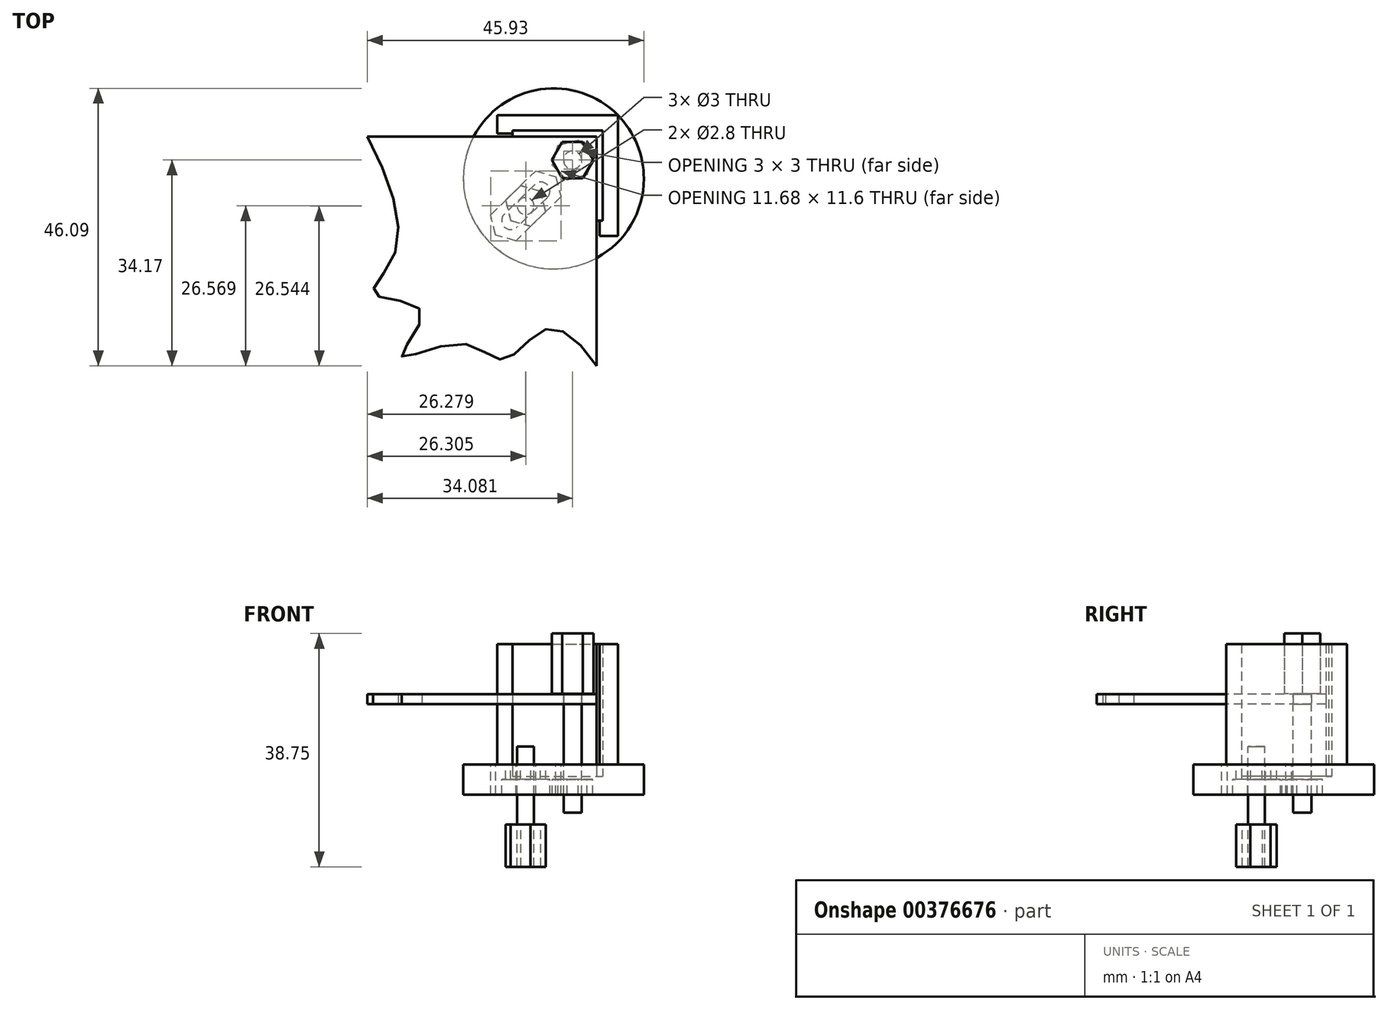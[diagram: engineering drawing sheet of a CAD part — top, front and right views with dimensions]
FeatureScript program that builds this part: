
annotation { "Feature Type Name" : "Feature", "Feature Type Description" : "" }
export const myFeature = defineFeature(function(context is Context, id is Id, definition is map)
    precondition{}
    {
        {
            var Q0;
            Q0=qCreatedBy(makeId("Top.planeOp"),FACE);
            var sketch = newSketch(context, id + "F0", { "sketchPlane" : qUnion([Q0])});
            skCircle(sketch, "E0", {"center": v(0, 0) * mm, "radius": 15 * mm});
            skLineSegment(sketch, "E1.bottom", {"start": v(-6.85, 7.99) * mm, "end": v(8.15, 7.99) * mm});
            skLineSegment(sketch, "E1.right", {"start": v(8.15, 7.99) * mm, "end": v(8.15, -7.01) * mm});
            skLineSegment(sketch, "E2.0", {"start": v(7.15, 6.99) * mm, "end": v(7.15, -7.01) * mm});
            skLineSegment(sketch, "E2.1", {"start": v(-6.85, 6.99) * mm, "end": v(7.15, 6.99) * mm});
            skLineSegment(sketch, "E3", {"start": v(-2.12, -2.07) * mm, "end": v(-7.13, -6.97) * mm, "construction": true});
            skArc(sketch, "E4.0.startCap", {"start": v(-3.17, -1) * mm, "mid": v(-1.05, -1.03) * mm, "end": v(-1.07, -3.15) * mm});
            skArc(sketch, "E4.0.endCap", {"start": v(-6.08, -8.04) * mm, "mid": v(-8.2, -8.02) * mm, "end": v(-8.18, -5.9) * mm});
            skLineSegment(sketch, "E4.0.left", {"start": v(-1.07, -3.15) * mm, "end": v(-6.08, -8.04) * mm});
            skLineSegment(sketch, "E4.0.right", {"start": v(-3.17, -1) * mm, "end": v(-8.18, -5.9) * mm});
            skLineSegment(sketch, "E5", {"start": v(0.02, 0.02) * mm, "end": v(17.55, 17.15) * mm, "construction": true});
            skLineSegment(sketch, "E6", {"start": v(-6.85, 6.99) * mm, "end": v(-6.85, 7.99) * mm});
            skLineSegment(sketch, "E7", {"start": v(7.15, -7.01) * mm, "end": v(8.15, -7.01) * mm});
            skLineSegment(sketch, "E8.0", {"start": v(-9.38, 7.49) * mm, "end": v(-9.38, 10.52) * mm});
            skLineSegment(sketch, "E8.1", {"start": v(10.69, 10.52) * mm, "end": v(10.69, -9.55) * mm});
            skLineSegment(sketch, "E8.2", {"start": v(7.65, -9.55) * mm, "end": v(10.69, -9.55) * mm});
            skLineSegment(sketch, "E8.3", {"start": v(-9.38, 10.52) * mm, "end": v(10.69, 10.52) * mm});
            skPoint(sketch, "E9.endSnap0", {"position": v(-9.38, 7.49) * mm});
            skPoint(sketch, "E10.orphan", {"position": v(-9.38, 4.45) * mm});
            skLineSegment(sketch, "E11", {"start": v(7.65, -7.01) * mm, "end": v(7.65, -9.55) * mm});
            skLineSegment(sketch, "E12", {"start": v(-6.85, 7.49) * mm, "end": v(-9.38, 7.49) * mm});
            skPoint(sketch, "E9.end.orphan", {"position": v(-9.38, 7.07) * mm});
            skLineSegment(sketch, "E13", {"start": v(-2.12, -2.07) * mm, "end": v(0, 0) * mm, "construction": true});
            skCircle(sketch, "E14", {"center": v(3.15, 3.08) * mm, "radius": 1.5 * mm});
            skCircle(sketch, "E15.cCircle", {"center": v(-7.13, -6.97) * mm, "radius": 3 * mm, "construction": true});
            skLineSegment(sketch, "E15.0", {"start": v(-5.03, -9.11) * mm, "end": v(-6.27, -10.32) * mm});
            skLineSegment(sketch, "E15.1", {"start": v(-6.27, -10.32) * mm, "end": v(-9.6, -9.39) * mm});
            skLineSegment(sketch, "E15.2", {"start": v(-9.6, -9.39) * mm, "end": v(-10.46, -6.03) * mm});
            skLineSegment(sketch, "E15.3", {"start": v(-10.46, -6.03) * mm, "end": v(-9.23, -4.82) * mm});
            skPoint(sketch, "E15.0.midPoint", {"position": v(-5.03, -9.11) * mm});
            skCircle(sketch, "E16.cCircle", {"center": v(-2.12, -2.07) * mm, "radius": 3 * mm, "construction": true});
            skLineSegment(sketch, "E16.0", {"start": v(1.21, -3) * mm, "end": v(-0.03, -4.22) * mm});
            skLineSegment(sketch, "E16.3", {"start": v(-4.22, 0.07) * mm, "end": v(-2.98, 1.28) * mm});
            skLineSegment(sketch, "E16.4", {"start": v(-2.98, 1.28) * mm, "end": v(0.36, 0.35) * mm});
            skLineSegment(sketch, "E16.5", {"start": v(0.36, 0.35) * mm, "end": v(1.21, -3) * mm});
            skPoint(sketch, "E16.0.midPoint", {"position": v(-0.03, -4.22) * mm});
            skPoint(sketch, "E17.orphan", {"position": v(-4.65, -4.55) * mm});
            skPoint(sketch, "E18.orphan", {"position": v(-3.8, -7.9) * mm});
            skLineSegment(sketch, "E19", {"start": v(-9.23, -4.82) * mm, "end": v(-4.22, 0.07) * mm});
            skLineSegment(sketch, "E20", {"start": v(-5.03, -9.11) * mm, "end": v(-0.03, -4.22) * mm});
            skSolve(sketch);
        }
        {
            var Q0;
            {var subQ4=sQuery(id+"F0.wireOp",EDGE,"E1.bottom");Q0=makeQuery(id+"F0.imprint","IMPRINT",FACE,{"disambiguationData":[TD([[makeQuery(id+"F0.imprint","IMPRINT",EDGE,{"derivedFrom":subQ4}),1.0]])]});}
            var Q1;
            Q1=makeQuery(id+"F0.imprint","IMPRINT",FACE,{"disambiguationData":[TD([[makeQuery(id+"F0.imprint","IMPRINT",EDGE,{"derivedFrom":sQuery(id+"F0.wireOp",EDGE,"E0")}),1.0]])]});
            var Q2;
            {var subQ3=sQuery(id+"F0.wireOp",EDGE,"E1.bottom");Q2=makeQuery(id+"F0.imprint","IMPRINT",FACE,{"disambiguationData":[TD([[makeQuery(id+"F0.imprint","IMPRINT",EDGE,{"derivedFrom":subQ3}),-1.0]])]});}
            var Q3;
            Q3=makeQuery(id+"F0.imprint","IMPRINT",FACE,{"disambiguationData":[TD([[makeQuery(id+"F0.imprint","IMPRINT",EDGE,{"derivedFrom":sQuery(id+"F0.wireOp",EDGE,"E4.0.startCap")}),1.0]])]});
            extrude(context, id + "F1", {"entities" : qUnion([Q0, Q1, Q2, Q3]), "oppositeDirection" : true, "depth" : 5 * mm, "offsetDistance" : 25 * mm});
        }
        {
            var Q0;
            {var subQ4=sQuery(id+"F0.wireOp",EDGE,"E1.bottom");Q0=makeQuery(id+"F0.imprint","IMPRINT",FACE,{"disambiguationData":[TD([[makeQuery(id+"F0.imprint","IMPRINT",EDGE,{"derivedFrom":subQ4}),1.0]])]});}
            extrude(context, id + "F2", {"entities" : qUnion([Q0]), "operationType" : NewBodyOperationType.ADD, "depth" : 20 * mm, "offsetDistance" : 25 * mm});
        }
        {
            var Q0;
            {var subQ3=sQuery(id+"F0.wireOp",EDGE,"E1.bottom");Q0=makeQuery(id+"F0.imprint","IMPRINT",FACE,{"disambiguationData":[TD([[makeQuery(id+"F0.imprint","IMPRINT",EDGE,{"derivedFrom":subQ3}),-1.0]])]});}
            extrude(context, id + "F3", {"entities" : qUnion([Q0]), "depth" : 20 * mm, "offsetDistance" : 25 * mm, "hasSecondDirection" : true, "secondDirectionOppositeDirection" : true, "secondDirectionDepth" : 2 * mm});
        }
        {
            var Q0;
            Q0=makeQuery(id+"F1.opExtrude","CAP_FACE",FACE,{"disambiguationData":[OSD([sQuery(id+"F0.wireOp",EDGE,"E0"),sQuery(id+"F0.wireOp",EDGE,"E4.0.startCap"),sQuery(id+"F0.wireOp",EDGE,"E4.0.endCap"),sQuery(id+"F0.wireOp",EDGE,"E4.0.left"),sQuery(id+"F0.wireOp",EDGE,"E4.0.right"),sQuery(id+"F0.wireOp",EDGE,"E14")])],"isStart":false});
            var sketch = newSketch(context, id + "F4", { "sketchPlane" : qUnion([Q0])});
            skPoint(sketch, "E21", {"position": v(3.15, -3.08) * mm});
            skCircle(sketch, "E22.cCircle", {"center": v(3.15, -3.08) * mm, "radius": 3 * mm, "construction": true});
            skLineSegment(sketch, "E22.0", {"start": v(6.5, -3.95) * mm, "end": v(4.07, -6.42) * mm});
            skLineSegment(sketch, "E22.1", {"start": v(4.07, -6.42) * mm, "end": v(0.72, -5.55) * mm});
            skLineSegment(sketch, "E22.2", {"start": v(0.72, -5.55) * mm, "end": v(-0.2, -2.2) * mm});
            skLineSegment(sketch, "E22.3", {"start": v(-0.2, -2.2) * mm, "end": v(2.23, 0.26) * mm});
            skLineSegment(sketch, "E22.4", {"start": v(2.23, 0.26) * mm, "end": v(5.58, -0.61) * mm});
            skLineSegment(sketch, "E22.5", {"start": v(5.58, -0.61) * mm, "end": v(6.5, -3.95) * mm});
            skPoint(sketch, "E22.0.midPoint", {"position": v(5.29, -5.19) * mm});
            skSolve(sketch);
        }
        {
            var Q0;
            Q0=makeQuery(id+"F4.imprint","IMPRINT",FACE,{"disambiguationData":[TD([[makeQuery(id+"F4.imprint","IMPRINT",EDGE,{"derivedFrom":sQuery(id+"F4.wireOp",EDGE,"E22.0")}),-1.0]])]});
            extrude(context, id + "F5", {"entities" : qUnion([Q0]), "operationType" : NewBodyOperationType.REMOVE, "oppositeDirection" : true, "depth" : 2.5 * mm, "offsetDistance" : 25 * mm});
        }
        {
            var Q0;
            Q0=makeQuery(id+"F0.imprint","IMPRINT",FACE,{"disambiguationData":[TD([[makeQuery(id+"F0.imprint","IMPRINT",EDGE,{"derivedFrom":sQuery(id+"F0.wireOp",EDGE,"E4.0.startCap")}),1.0]])]});
            extrude(context, id + "F6", {"entities" : qUnion([Q0]), "operationType" : NewBodyOperationType.REMOVE, "oppositeDirection" : true, "depth" : 2.5 * mm, "offsetDistance" : 25 * mm});
        }
        {
            var Q0;
            Q0=makeQuery(id+"F0.imprint","IMPRINT",FACE,{"disambiguationData":[TD([[makeQuery(id+"F0.imprint","IMPRINT",EDGE,{"derivedFrom":sQuery(id+"F0.wireOp",EDGE,"E0")}),1.0]])]});
            cPlane(context, id + "F7", {"entities" : qUnion([Q0]), "cplaneType" : CPlaneType.OFFSET, "offset" : 10 * mm, "width" : 150 * mm, "height" : 150 * mm});
        }
        {
            var Q0;
            Q0=qCreatedBy(id+"F7.planeOp",FACE);
            var sketch = newSketch(context, id + "F8", { "sketchPlane" : qUnion([Q0])});
            skLineSegment(sketch, "E23.bottom", {"start": v(7.15, 6.99) * mm, "end": v(-30.93, 6.99) * mm});
            skLineSegment(sketch, "E23.left", {"start": v(7.15, 6.99) * mm, "end": v(7.15, -31.1) * mm});
            skFitSpline(sketch, "E24", {"points": [v(-30.93, 6.99) * mm, v(-26.55, -12.85) * mm, v(-29.76, -19.17) * mm, v(-21.98, -22.11) * mm, v(-25.26, -29.41) * mm, v(-15.4, -27.41) * mm, v(-8.13, -30.02) * mm, v(-1.2, -25.01) * mm, v(7.15, -31.1) * mm], "startDerivative": vector(61.2, -118.32) * mm, "endDerivative": vector(56.82, -85.75) * mm});
            skCircle(sketch, "E25.0", {"center": v(3.15, 3.08) * mm, "radius": 1.5 * mm});
            skSolve(sketch);
        }
        {
            var Q0;
            Q0=makeQuery(id+"F8.imprint","IMPRINT",FACE,{"disambiguationData":[TD([[makeQuery(id+"F8.imprint","IMPRINT",EDGE,{"derivedFrom":sQuery(id+"F8.wireOp",EDGE,"E23.bottom")}),1.0]])]});
            extrude(context, id + "F9", {"entities" : qUnion([Q0]), "depth" : 1.7 * mm, "offsetDistance" : 25 * mm});
        }
        {
            var Q0;
            Q0=makeQuery(id+"F0.imprint","IMPRINT",FACE,{"disambiguationData":[TD([[makeQuery(id+"F0.imprint","IMPRINT",EDGE,{"derivedFrom":sQuery(id+"F0.wireOp",EDGE,"E0")}),1.0]])]});
            var sketch = newSketch(context, id + "F10", { "sketchPlane" : qUnion([Q0])});
            skPoint(sketch, "E26.0", {"position": v(-4.65, -4.55) * mm});
            skCircle(sketch, "E27", {"center": v(-4.65, -4.55) * mm, "radius": 1.4 * mm});
            skCircle(sketch, "E28.cCircle", {"center": v(-4.65, -4.55) * mm, "radius": 3 * mm, "construction": true});
            skLineSegment(sketch, "E28.0", {"start": v(-1.32, -5.48) * mm, "end": v(-3.8, -7.9) * mm});
            skLineSegment(sketch, "E28.1", {"start": v(-3.8, -7.9) * mm, "end": v(-7.13, -6.97) * mm});
            skLineSegment(sketch, "E28.2", {"start": v(-7.13, -6.97) * mm, "end": v(-7.99, -3.61) * mm});
            skLineSegment(sketch, "E28.3", {"start": v(-7.99, -3.61) * mm, "end": v(-5.5, -1.19) * mm});
            skLineSegment(sketch, "E28.4", {"start": v(-5.5, -1.19) * mm, "end": v(-2.17, -2.12) * mm});
            skLineSegment(sketch, "E28.5", {"start": v(-2.17, -2.12) * mm, "end": v(-1.32, -5.48) * mm});
            skPoint(sketch, "E28.0.midPoint", {"position": v(-2.58, -6.67) * mm});
            skSolve(sketch);
        }
        {
            var Q0;
            Q0 = qSketchRegion(id + "F10", true);
            var Q1;
            Q1=makeQuery(id+"F6.boolean.opBoolean","COPY",FACE,{"derivedFrom":makeQuery(id+"F6.opExtrude","CAP_FACE",FACE,{"disambiguationData":[OSD([sQuery(id+"F0.wireOp",EDGE,"E4.0.startCap"),sQuery(id+"F0.wireOp",EDGE,"E4.0.endCap"),sQuery(id+"F0.wireOp",EDGE,"E4.0.left"),sQuery(id+"F0.wireOp",EDGE,"E4.0.right"),sQuery(id+"F0.wireOp",EDGE,"E15.0"),sQuery(id+"F0.wireOp",EDGE,"E15.1"),sQuery(id+"F0.wireOp",EDGE,"E15.2"),sQuery(id+"F0.wireOp",EDGE,"E15.3"),sQuery(id+"F0.wireOp",EDGE,"E16.0"),sQuery(id+"F0.wireOp",EDGE,"E16.3"),sQuery(id+"F0.wireOp",EDGE,"E16.4"),sQuery(id+"F0.wireOp",EDGE,"E16.5"),sQuery(id+"F0.wireOp",EDGE,"E19"),sQuery(id+"F0.wireOp",EDGE,"E20")])],"isStart":false})});
            extrude(context, id + "F11", {"entities" : qUnion([Q0]), "endBound" : BoundingType.UP_TO_SURFACE, "oppositeDirection" : true, "depth" : 25 * mm, "endBoundEntityFace" : qUnion([Q1]), "offsetDistance" : 25 * mm});
        }
        {
            var Q0;
            Q0=makeQuery(id+"F0.imprint","IMPRINT",FACE,{"disambiguationData":[TD([[makeQuery(id+"F0.imprint","IMPRINT",EDGE,{"derivedFrom":sQuery(id+"F0.wireOp",EDGE,"E0")}),1.0]])]});
            var sketch = newSketch(context, id + "F12", { "sketchPlane" : qUnion([Q0])});
            skCircle(sketch, "E29.0", {"center": v(-4.65, -4.55) * mm, "radius": 1.4 * mm});
            skSolve(sketch);
        }
        {
            var Q0;
            Q0=makeQuery(id+"F12.imprint","IMPRINT",FACE,{"disambiguationData":[TD([[makeQuery(id+"F12.imprint","IMPRINT",EDGE,{"derivedFrom":sQuery(id+"F12.wireOp",EDGE,"E29.0")}),1.0]])]});
            extrude(context, id + "F13", {"entities" : qUnion([Q0]), "oppositeDirection" : true, "depth" : 10 * mm, "offsetDistance" : 25 * mm, "hasSecondDirection" : true, "secondDirectionOppositeDirection" : false, "secondDirectionDepth" : 3 * mm});
        }
        {
            var Q0;
            Q0=makeQuery(id+"F13.opExtrude","CAP_FACE",FACE,{"disambiguationData":[OSD([sQuery(id+"F12.wireOp",EDGE,"E29.0")])],"isStart":false});
            var sketch = newSketch(context, id + "F14", { "sketchPlane" : qUnion([Q0])});
            skCircle(sketch, "E30.cCircle", {"center": v(-4.65, 4.55) * mm, "radius": 3 * mm, "construction": true});
            skLineSegment(sketch, "E30.0", {"start": v(-3.85, 7.92) * mm, "end": v(-1.33, 5.54) * mm});
            skLineSegment(sketch, "E30.1", {"start": v(-1.33, 5.54) * mm, "end": v(-2.13, 2.17) * mm});
            skLineSegment(sketch, "E30.2", {"start": v(-2.13, 2.17) * mm, "end": v(-5.45, 1.17) * mm});
            skLineSegment(sketch, "E30.3", {"start": v(-5.45, 1.17) * mm, "end": v(-7.97, 3.55) * mm});
            skLineSegment(sketch, "E30.4", {"start": v(-7.97, 3.55) * mm, "end": v(-7.17, 6.92) * mm});
            skLineSegment(sketch, "E30.5", {"start": v(-7.17, 6.92) * mm, "end": v(-3.85, 7.92) * mm});
            skPoint(sketch, "E30.0.midPoint", {"position": v(-2.6, 6.73) * mm});
            skSolve(sketch);
        }
        {
            var Q0;
            Q0=makeQuery(id+"F14.imprint","IMPRINT",FACE,{"disambiguationData":[TD([[makeQuery(id+"F14.imprint","IMPRINT",EDGE,{"derivedFrom":sQuery(id+"F14.wireOp",EDGE,"E30.0")}),-1.0]])]});
            extrude(context, id + "F15", {"entities" : qUnion([Q0]), "operationType" : NewBodyOperationType.ADD, "depth" : 7 * mm, "offsetDistance" : 25 * mm});
        }
        {
            var Q0;
            Q0=makeQuery(id+"F5.boolean.opBoolean","COPY",FACE,{"derivedFrom":makeQuery(id+"F5.opExtrude","CAP_FACE",FACE,{"disambiguationData":[OSD([sQuery(id+"F0.wireOp",EDGE,"E14"),sQuery(id+"F4.wireOp",EDGE,"E22.0"),sQuery(id+"F4.wireOp",EDGE,"E22.1"),sQuery(id+"F4.wireOp",EDGE,"E22.2"),sQuery(id+"F4.wireOp",EDGE,"E22.3"),sQuery(id+"F4.wireOp",EDGE,"E22.4"),sQuery(id+"F4.wireOp",EDGE,"E22.5")])],"isStart":false})});
            var Q1;
            Q1=makeQuery(id+"F1.opExtrude","CAP_FACE",FACE,{"disambiguationData":[OSD([sQuery(id+"F0.wireOp",EDGE,"E0"),sQuery(id+"F0.wireOp",EDGE,"E4.0.startCap"),sQuery(id+"F0.wireOp",EDGE,"E4.0.endCap"),sQuery(id+"F0.wireOp",EDGE,"E4.0.left"),sQuery(id+"F0.wireOp",EDGE,"E4.0.right"),sQuery(id+"F0.wireOp",EDGE,"E14")])],"isStart":false});
            extrude(context, id + "F16", {"entities" : qUnion([Q0]), "endBound" : BoundingType.UP_TO_SURFACE, "depth" : 25 * mm, "endBoundEntityFace" : qUnion([Q1]), "offsetDistance" : 25 * mm});
        }
        {
            var Q0;
            Q0=makeQuery(id+"F1.opExtrude","CAP_FACE",FACE,{"disambiguationData":[OSD([sQuery(id+"F0.wireOp",EDGE,"E0"),sQuery(id+"F0.wireOp",EDGE,"E4.0.startCap"),sQuery(id+"F0.wireOp",EDGE,"E4.0.endCap"),sQuery(id+"F0.wireOp",EDGE,"E4.0.left"),sQuery(id+"F0.wireOp",EDGE,"E4.0.right"),sQuery(id+"F0.wireOp",EDGE,"E14")])],"isStart":false});
            var sketch = newSketch(context, id + "F17", { "sketchPlane" : qUnion([Q0])});
            skCircle(sketch, "E31.0", {"center": v(3.15, -3.08) * mm, "radius": 1.5 * mm});
            skSolve(sketch);
        }
        {
            var Q0;
            Q0=makeQuery(id+"F17.imprint","IMPRINT",FACE,{"disambiguationData":[TD([[makeQuery(id+"F17.imprint","IMPRINT",EDGE,{"derivedFrom":sQuery(id+"F17.wireOp",EDGE,"E31.0")}),1.0]])]});
            extrude(context, id + "F18", {"entities" : qUnion([Q0]), "depth" : 3 * mm, "offsetDistance" : 25 * mm, "hasSecondDirection" : true, "secondDirectionOppositeDirection" : true, "secondDirectionDepth" : 16.75 * mm});
        }
        {
            var Q0;
            Q0=makeQuery(id+"F18.opExtrude","CAP_FACE",FACE,{"disambiguationData":[OSD([sQuery(id+"F17.wireOp",EDGE,"E31.0")])],"isStart":true});
            var sketch = newSketch(context, id + "F19", { "sketchPlane" : qUnion([Q0])});
            skCircle(sketch, "E32.cCircle", {"center": v(3.15, 3.08) * mm, "radius": 3 * mm, "construction": true});
            skLineSegment(sketch, "E32.0", {"start": v(4.88, 0.08) * mm, "end": v(1.42, 0.08) * mm});
            skLineSegment(sketch, "E32.1", {"start": v(1.42, 0.08) * mm, "end": v(-0.31, 3.08) * mm});
            skLineSegment(sketch, "E32.2", {"start": v(-0.31, 3.08) * mm, "end": v(1.42, 6.08) * mm});
            skLineSegment(sketch, "E32.3", {"start": v(1.42, 6.08) * mm, "end": v(4.88, 6.08) * mm});
            skLineSegment(sketch, "E32.4", {"start": v(4.88, 6.08) * mm, "end": v(6.62, 3.08) * mm});
            skLineSegment(sketch, "E32.5", {"start": v(6.62, 3.08) * mm, "end": v(4.88, 0.08) * mm});
            skPoint(sketch, "E32.0.midPoint", {"position": v(3.15, 0.08) * mm});
            skSolve(sketch);
        }
        {
            var Q0;
            Q0=makeQuery(id+"F19.imprint","IMPRINT",FACE,{"disambiguationData":[TD([[makeQuery(id+"F19.imprint","IMPRINT",EDGE,{"derivedFrom":sQuery(id+"F19.wireOp",EDGE,"E32.0")}),-1.0]])]});
            var Q1;
            Q1=makeQuery(id+"F19.imprint","IMPRINT",FACE,{"disambiguationData":[TD([[makeQuery(id+"F19.imprint","IMPRINT",EDGE,{"derivedFrom":makeQuery(id+"F18.opExtrude","CAP_EDGE",EDGE,{"disambiguationData":[OSD([sQuery(id+"F17.wireOp",EDGE,"E31.0")])],"isStart":true})}),-1.0]])]});
            extrude(context, id + "F20", {"entities" : qUnion([Q0, Q1]), "operationType" : NewBodyOperationType.ADD, "depth" : 10 * mm, "offsetDistance" : 25 * mm});
        }
        {
            var Q0;
            Q0=makeQuery(id+"F3.opExtrude","SWEPT_BODY",BODY,{"disambiguationData":[OSD([sQuery(id+"F0.wireOp",EDGE,"E1.bottom"),sQuery(id+"F0.wireOp",EDGE,"E1.right"),sQuery(id+"F0.wireOp",EDGE,"E2.0"),sQuery(id+"F0.wireOp",EDGE,"E2.1"),sQuery(id+"F0.wireOp",EDGE,"E6"),sQuery(id+"F0.wireOp",EDGE,"E7")])]});
            var Q1;
            Q1=makeQuery(id+"F1.opExtrude","SWEPT_BODY",BODY,{"disambiguationData":[OSD([sQuery(id+"F0.wireOp",EDGE,"E0"),sQuery(id+"F0.wireOp",EDGE,"E4.0.startCap"),sQuery(id+"F0.wireOp",EDGE,"E4.0.endCap"),sQuery(id+"F0.wireOp",EDGE,"E4.0.left"),sQuery(id+"F0.wireOp",EDGE,"E4.0.right"),sQuery(id+"F0.wireOp",EDGE,"E14")])]});
            booleanBodies(context, id + "F21", {"operationType" : BooleanOperationType.SUBTRACTION, "tools" : qUnion([Q0]), "targets" : qUnion([Q1]), "keepTools" : true});
        }
    });
